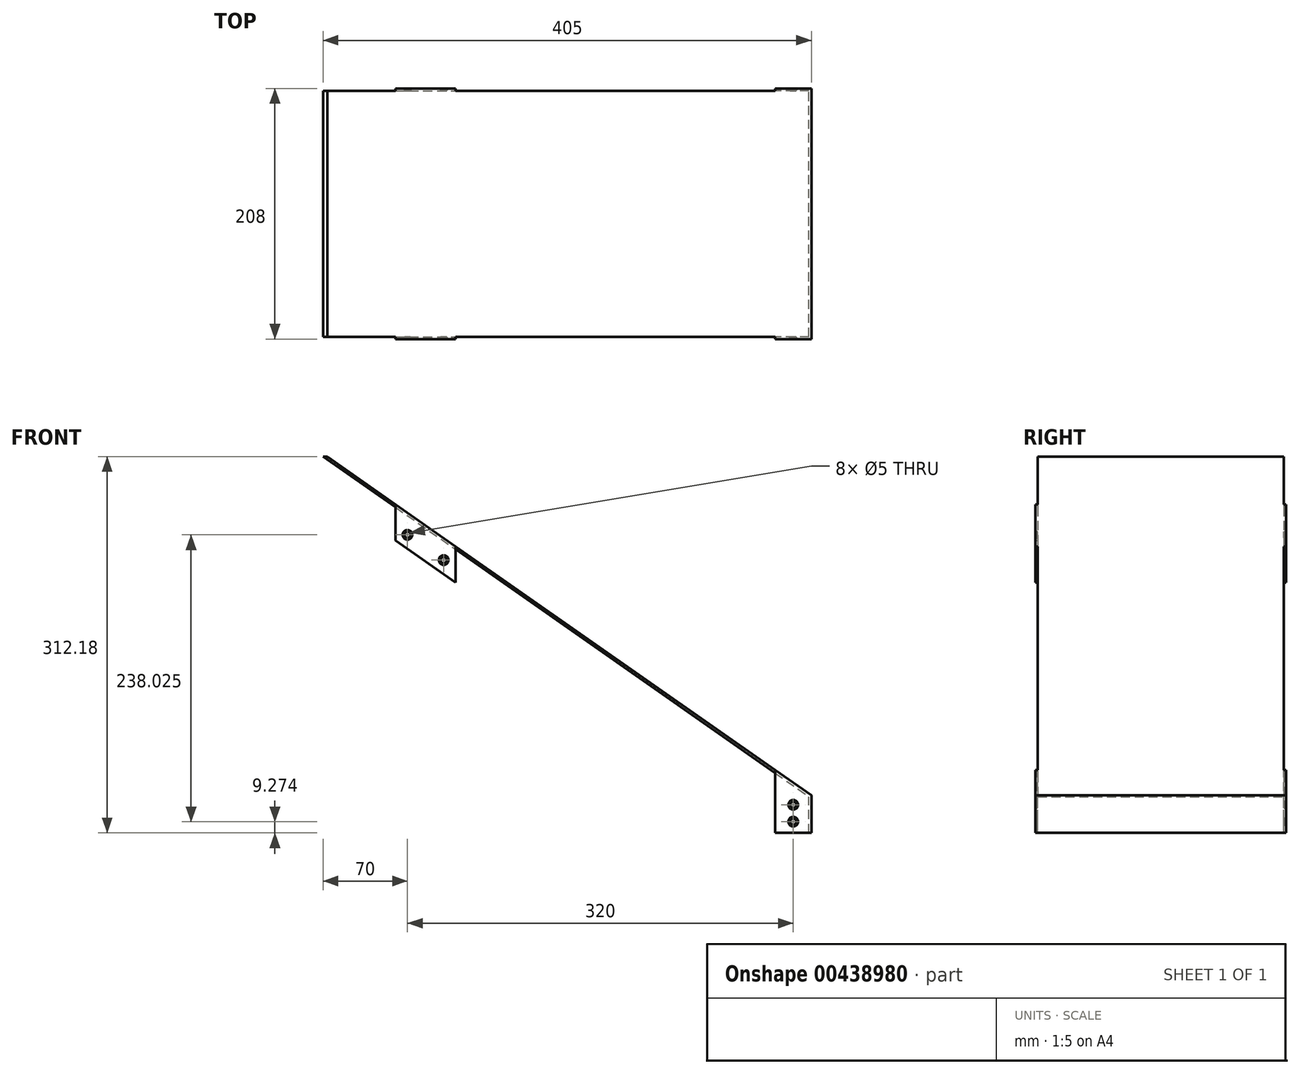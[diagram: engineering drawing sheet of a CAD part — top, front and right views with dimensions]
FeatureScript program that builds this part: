
annotation { "Feature Type Name" : "Feature", "Feature Type Description" : "" }
export const myFeature = defineFeature(function(context is Context, id is Id, definition is map)
    precondition{}
    {
        {
            var Q0;
            Q0=qCreatedBy(makeId("Front.planeOp"),FACE);
            var sketch = newSketch(context, id + "F0", { "sketchPlane" : qUnion([Q0])});
            skLineSegment(sketch, "E0", {"start": v(30, 31.04) * mm, "end": v(30, 0) * mm});
            skLineSegment(sketch, "E1", {"start": v(28, 0) * mm, "end": v(28, 30) * mm});
            skLineSegment(sketch, "E2", {"start": v(-375, 312.18) * mm, "end": v(28, 30) * mm});
            skLineSegment(sketch, "E3", {"start": v(28, 0) * mm, "end": v(30, 0) * mm});
            skLineSegment(sketch, "E4", {"start": v(30, 31.04) * mm, "end": v(-371.51, 312.18) * mm});
            skLineSegment(sketch, "E5", {"start": v(-371.51, 312.18) * mm, "end": v(-375, 312.18) * mm});
            skSolve(sketch);
        }
        {
            var Q0;
            Q0 = qSketchRegion(id + "F0", true);
            extrude(context, id + "F1", {"entities" : qUnion([Q0]), "depth" : 204 * mm});
        }
        {
            var Q0;
            Q0=qCreatedBy(makeId("Front.planeOp"),FACE);
            cPlane(context, id + "F2", {"entities" : qUnion([Q0]), "cplaneType" : CPlaneType.OFFSET, "offset" : 102 * mm, "width" : 150 * mm, "height" : 150 * mm});
        }
        {
            var Q0;
            Q0=qCreatedBy(makeId("Front.planeOp"),FACE);
            cPlane(context, id + "F3", {"entities" : qUnion([Q0]), "cplaneType" : CPlaneType.OFFSET, "offset" : 204 * mm, "width" : 150 * mm, "height" : 150 * mm});
        }
        {
            var Q0;
            Q0=qCreatedBy(id+"F3.planeOp",FACE);
            var sketch = newSketch(context, id + "F4", { "sketchPlane" : qUnion([Q0])});
            skLineSegment(sketch, "E6", {"start": v(0, 0) * mm, "end": v(0, 52.05) * mm});
            skLineSegment(sketch, "E7", {"start": v(0, 52.05) * mm, "end": v(30, 31.04) * mm});
            skLineSegment(sketch, "E8", {"start": v(30, 31.04) * mm, "end": v(30, 0) * mm});
            skLineSegment(sketch, "E9", {"start": v(30, 0) * mm, "end": v(0, 0) * mm});
            skLineSegment(sketch, "E10", {"start": v(-315, 272.61) * mm, "end": v(-315, 242.61) * mm});
            skLineSegment(sketch, "E11", {"start": v(-315, 242.61) * mm, "end": v(-265, 207.6) * mm});
            skLineSegment(sketch, "E12", {"start": v(-265, 207.6) * mm, "end": v(-265, 237.6) * mm});
            skLineSegment(sketch, "E13", {"start": v(-315, 272.61) * mm, "end": v(-265, 237.6) * mm});
            skSolve(sketch);
        }
        {
            var Q0;
            Q0 = qSketchRegion(id + "F4", true);
            extrude(context, id + "F5", {"entities" : qUnion([Q0]), "operationType" : NewBodyOperationType.ADD, "depth" : 2 * mm});
        }
        {
            var Q0;
            Q0=makeQuery(id+"F5.opExtrude","CAP_FACE",FACE,{"disambiguationData":[OSD([sQuery(id+"F4.wireOp",EDGE,"E6"),sQuery(id+"F4.wireOp",EDGE,"E7"),sQuery(id+"F4.wireOp",EDGE,"E8"),sQuery(id+"F4.wireOp",EDGE,"E9")])],"isStart":false});
            var sketch = newSketch(context, id + "F6", { "sketchPlane" : qUnion([Q0])});
            skLineSegment(sketch, "E14", {"start": v(0, 0) * mm, "end": v(30, 0) * mm, "construction": true});
            skLineSegment(sketch, "E15", {"start": v(15, 0) * mm, "end": v(15, 31.27) * mm, "construction": true});
            skPoint(sketch, "E15.endSnap0", {"position": v(15, 38.27) * mm});
            skLineSegment(sketch, "E16", {"start": v(30, 31.27) * mm, "end": v(0, 31.27) * mm, "construction": true});
            skPoint(sketch, "E17", {"position": v(15, 31.27) * mm});
            skLineSegment(sketch, "E18", {"start": v(15, 16.27) * mm, "end": v(-5.95, 16.27) * mm, "construction": true});
            skLineSegment(sketch, "E19.trimOffspring", {"start": v(15, 38.27) * mm, "end": v(15, 62.55) * mm, "construction": true});
            skPoint(sketch, "E20", {"position": v(15, 23.27) * mm});
            skPoint(sketch, "E21.MirrorP", {"position": v(15, 9.27) * mm});
            skPoint(sketch, "E22", {"position": v(-305, 247.3) * mm});
            skPoint(sketch, "E23", {"position": v(-275, 226.3) * mm});
            skSolve(sketch);
        }
        {
            var Q0;
            Q0=sQuery(id+"F6.wireOp",VERTEX,"E20");
            var Q1;
            Q1=sQuery(id+"F6.wireOp",VERTEX,"E21.MirrorP");
            var Q2;
            Q2=makeQuery(id+"F1.opExtrude","SWEPT_BODY",BODY,{"disambiguationData":[OSD([sQuery(id+"F0.wireOp",EDGE,"E0"),sQuery(id+"F0.wireOp",EDGE,"E1"),sQuery(id+"F0.wireOp",EDGE,"jMCN8mi6-JGkK-3KeV-axMJ-rePCCD6Ndh63"),sQuery(id+"F0.wireOp",EDGE,"zP6et7PR-J7rC-ssxN-R9dq-NqHO7dBge2xO"),sQuery(id+"F0.wireOp",EDGE,"E2"),sQuery(id+"F0.wireOp",EDGE,"E3")])]});
            hole(context, id + "F7", {"style" : HoleStyle.C_SINK, "endStyle" : HoleEndStyle.BLIND, "holeDiameter" : 5 * mm, "cSinkDiameter" : 8 * mm, "cSinkAngle" : 90 * degree, "holeDepth" : 10 * mm, "isTappedThrough" : true, "tappedDepth" : 12 * mm, "tapClearance" : 3, "startFromSketch" : true, "locations" : qUnion([Q0, Q1]), "scope" : qUnion([Q2])});
        }
        {
            var Q0;
            Q0=sQuery(id+"F6.wireOp",VERTEX,"E22");
            var Q1;
            Q1=sQuery(id+"F6.wireOp",VERTEX,"E23");
            var Q2;
            Q2=makeQuery(id+"F1.opExtrude","SWEPT_BODY",BODY,{"disambiguationData":[OSD([sQuery(id+"F0.wireOp",EDGE,"E0"),sQuery(id+"F0.wireOp",EDGE,"E1"),sQuery(id+"F0.wireOp",EDGE,"jMCN8mi6-JGkK-3KeV-axMJ-rePCCD6Ndh63"),sQuery(id+"F0.wireOp",EDGE,"zP6et7PR-J7rC-ssxN-R9dq-NqHO7dBge2xO"),sQuery(id+"F0.wireOp",EDGE,"E2"),sQuery(id+"F0.wireOp",EDGE,"E3")])]});
            hole(context, id + "F8", {"style" : HoleStyle.C_SINK, "endStyle" : HoleEndStyle.BLIND, "holeDiameter" : 5 * mm, "cSinkDiameter" : 8 * mm, "cSinkAngle" : 90 * degree, "holeDepth" : 10 * mm, "isTappedThrough" : true, "tappedDepth" : 12 * mm, "tapClearance" : 3, "startFromSketch" : true, "locations" : qUnion([Q0, Q1]), "scope" : qUnion([Q2])});
        }
        {
            var Q0;
            Q0=makeQuery(id+"F1.opExtrude","SWEPT_BODY",BODY,{"disambiguationData":[OSD([sQuery(id+"F0.wireOp",EDGE,"E0"),sQuery(id+"F0.wireOp",EDGE,"E1"),sQuery(id+"F0.wireOp",EDGE,"jMCN8mi6-JGkK-3KeV-axMJ-rePCCD6Ndh63"),sQuery(id+"F0.wireOp",EDGE,"zP6et7PR-J7rC-ssxN-R9dq-NqHO7dBge2xO"),sQuery(id+"F0.wireOp",EDGE,"E2"),sQuery(id+"F0.wireOp",EDGE,"E3")])]});
            var Q1;
            Q1=qCreatedBy(id+"F2.planeOp",FACE);
            mirror(context, id + "F9", {"operationType" : NewBodyOperationType.ADD, "entities" : qUnion([Q0]), "mirrorPlane" : qUnion([Q1])});
        }
    });
